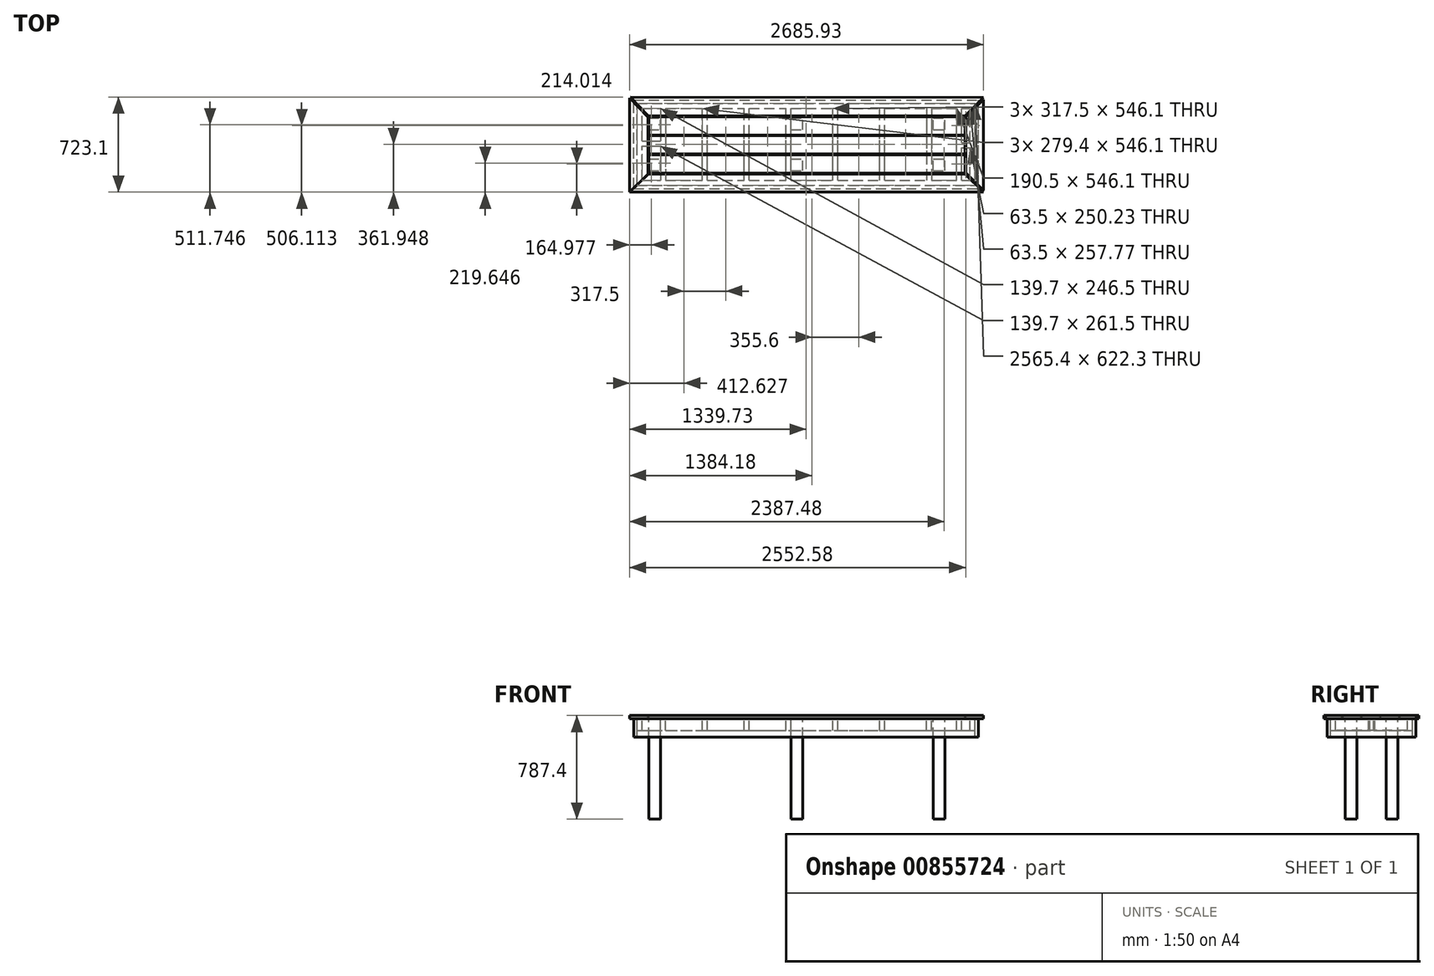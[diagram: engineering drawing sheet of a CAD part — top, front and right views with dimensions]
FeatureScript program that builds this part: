
annotation { "Feature Type Name" : "Feature", "Feature Type Description" : "" }
export const myFeature = defineFeature(function(context is Context, id is Id, definition is map)
    precondition{}
    {
        {
            var Q0;
            Q0=qCreatedBy(makeId("Top.planeOp"),FACE);
            var sketch = newSketch(context, id + "F0", { "sketchPlane" : qUnion([Q0])});
            skPoint(sketch, "E0.middle", {"position": v(0, 0) * mm});
            skLineSegment(sketch, "E1.bottom", {"start": v(-1467.07, -360.9) * mm, "end": v(1218.86, -360.9) * mm});
            skLineSegment(sketch, "E1.top", {"start": v(-1324.2, -222.85) * mm, "end": v(1080.8, -222.85) * mm});
            skLineSegment(sketch, "E2.0.1.0", {"start": v(-1321.05, -215.9) * mm, "end": v(1080.77, -215.9) * mm});
            skLineSegment(sketch, "E2.0.1.3", {"start": v(-1321.05, -76.2) * mm, "end": v(1080.04, -76.2) * mm});
            skLineSegment(sketch, "E2.0.2.0", {"start": v(-1321.05, -69.85) * mm, "end": v(1080, -69.85) * mm});
            skLineSegment(sketch, "E2.0.2.1", {"start": v(-1321.05, -69.85) * mm, "end": v(-1321.05, 69.85) * mm});
            skLineSegment(sketch, "E2.0.2.3", {"start": v(-1321.05, 69.85) * mm, "end": v(1079.27, 69.85) * mm});
            skLineSegment(sketch, "E2.0.3.0", {"start": v(-1321.05, 72.52) * mm, "end": v(1079.26, 72.52) * mm});
            skLineSegment(sketch, "E2.0.3.1", {"start": v(-1321.05, 72.52) * mm, "end": v(-1321.05, 210.28) * mm});
            skLineSegment(sketch, "E2.0.3.3", {"start": v(-1321.05, 210.28) * mm, "end": v(1078.53, 212.22) * mm});
            skLineSegment(sketch, "E2.0.4.0", {"start": v(-1322.9, 218.56) * mm, "end": v(1078.5, 218.56) * mm});
            skLineSegment(sketch, "E2.0.4.3", {"start": v(-1460.39, 362.2) * mm, "end": v(1218.86, 358.54) * mm});
            skLineSegment(sketch, "E3", {"start": v(-1321.05, -215.9) * mm, "end": v(-1321.05, -76.2) * mm});
            skLineSegment(sketch, "E4", {"start": v(-1467.07, -360.9) * mm, "end": v(-1324.2, -222.85) * mm});
            skLineSegment(sketch, "E5", {"start": v(-1326.9, -222.85) * mm, "end": v(-1467.07, -358.3) * mm});
            skLineSegment(sketch, "E6", {"start": v(-1467.07, 356.33) * mm, "end": v(-1467.07, -358.3) * mm});
            skLineSegment(sketch, "E7", {"start": v(-1327.27, 210.28) * mm, "end": v(-1467.07, 356.33) * mm});
            skLineSegment(sketch, "E8.trimOffspring", {"start": v(-1327.27, 210.28) * mm, "end": v(-1326.9, -222.85) * mm});
            skLineSegment(sketch, "E9", {"start": v(-1322.9, 218.56) * mm, "end": v(-1460.39, 362.2) * mm});
            skLineSegment(sketch, "E10", {"start": v(1218.86, -583.73) * mm, "end": v(1218.86, 490.14) * mm, "construction": true});
            skLineSegment(sketch, "E11", {"start": v(1218.86, -360.9) * mm, "end": v(1080.8, -222.85) * mm});
            skLineSegment(sketch, "E12", {"start": v(1218.86, 358.54) * mm, "end": v(1078.5, 218.56) * mm});
            skLineSegment(sketch, "E13", {"start": v(1080.77, -215.9) * mm, "end": v(1080.04, -76.2) * mm});
            skLineSegment(sketch, "E14.trimOffspring", {"start": v(1080, -69.85) * mm, "end": v(1079.27, 69.85) * mm});
            skLineSegment(sketch, "E15.trimOffspring", {"start": v(1079.26, 72.52) * mm, "end": v(1078.53, 212.22) * mm});
            skLineSegment(sketch, "E16", {"start": v(1086.83, -213.78) * mm, "end": v(1086.83, 211.28) * mm});
            skLineSegment(sketch, "E17", {"start": v(1086.83, 211.28) * mm, "end": v(1218.86, 342.95) * mm});
            skLineSegment(sketch, "E18", {"start": v(1086.83, -213.78) * mm, "end": v(1218.86, -345.8) * mm});
            skLineSegment(sketch, "E19", {"start": v(1218.86, -345.8) * mm, "end": v(1218.86, 342.95) * mm});
            skSolve(sketch);
        }
        {
            var Q0;
            Q0=makeQuery(id+"F0.imprint","IMPRINT",FACE,{"disambiguationData":[TD([[makeQuery(id+"F0.imprint","IMPRINT",EDGE,{"derivedFrom":sQuery(id+"F0.wireOp",EDGE,"HLl6yULO-rDhl-Czzw-94Pt-A62qj8Q72CLZ.bottom")}),-1.0]])]});
            var Q1;
            Q1=makeQuery(id+"F0.imprint","IMPRINT",FACE,{"disambiguationData":[TD([[makeQuery(id+"F0.imprint","IMPRINT",EDGE,{"derivedFrom":sQuery(id+"F0.wireOp",EDGE,"Z4ndjies-lr78-bC8g-xYQz-iFGjXOHwJ4Z8.bottom")}),1.0]])]});
            var Q2;
            Q2=makeQuery(id+"F0.imprint","IMPRINT",FACE,{"disambiguationData":[TD([[makeQuery(id+"F0.imprint","IMPRINT",EDGE,{"derivedFrom":sQuery(id+"F0.wireOp",EDGE,"E1.bottom")}),1.0]])]});
            var Q3;
            Q3=makeQuery(id+"F0.imprint","IMPRINT",FACE,{"disambiguationData":[TD([[makeQuery(id+"F0.imprint","IMPRINT",EDGE,{"derivedFrom":sQuery(id+"F0.wireOp",EDGE,"E2.0.1.0")}),1.0]])]});
            var Q4;
            Q4=makeQuery(id+"F0.imprint","IMPRINT",FACE,{"disambiguationData":[TD([[makeQuery(id+"F0.imprint","IMPRINT",EDGE,{"derivedFrom":sQuery(id+"F0.wireOp",EDGE,"E2.0.2.0")}),1.0]])]});
            var Q5;
            Q5=makeQuery(id+"F0.imprint","IMPRINT",FACE,{"disambiguationData":[TD([[makeQuery(id+"F0.imprint","IMPRINT",EDGE,{"derivedFrom":sQuery(id+"F0.wireOp",EDGE,"E2.0.3.0")}),1.0]])]});
            var Q6;
            Q6=makeQuery(id+"F0.imprint","IMPRINT",FACE,{"disambiguationData":[TD([[makeQuery(id+"F0.imprint","IMPRINT",EDGE,{"derivedFrom":sQuery(id+"F0.wireOp",EDGE,"E2.0.4.0")}),1.0]])]});
            var Q7;
            Q7=makeQuery(id+"F0.imprint","IMPRINT",FACE,{"disambiguationData":[TD([[makeQuery(id+"F0.imprint","IMPRINT",EDGE,{"derivedFrom":sQuery(id+"F0.wireOp",EDGE,"E5")}),-1.0]])]});
            var Q8;
            Q8=makeQuery(id+"F0.imprint","IMPRINT",FACE,{"disambiguationData":[TD([[makeQuery(id+"F0.imprint","IMPRINT",EDGE,{"derivedFrom":sQuery(id+"F0.wireOp",EDGE,"Z4ndjies-lr78-bC8g-xYQz-iFGjXOHwJ4Z8.left")}),-1.0]])]});
            var Q9;
            Q9=makeQuery(id+"F0.imprint","IMPRINT",FACE,{"disambiguationData":[TD([[makeQuery(id+"F0.imprint","IMPRINT",EDGE,{"derivedFrom":sQuery(id+"F0.wireOp",EDGE,"K0U2zqv0-DBfU-L3dn-5QTi-sevWSeDSVQ6E")}),1.0]])]});
            var Q10;
            Q10=makeQuery(id+"F0.imprint","IMPRINT",FACE,{"disambiguationData":[TD([[makeQuery(id+"F0.imprint","IMPRINT",EDGE,{"derivedFrom":sQuery(id+"F0.wireOp",EDGE,"E16")}),-1.0]])]});
            extrude(context, id + "F1", {"entities" : qUnion([Q0, Q1, Q2, Q3, Q4, Q5, Q6, Q7, Q8, Q9, Q10]), "oppositeDirection" : true, "depth" : 25.4 * mm, "offsetDistance" : 25.4 * mm});
        }
        {
            var Q0;
            Q0=makeQuery(id+"F1.opExtrude","CAP_FACE",FACE,{"disambiguationData":[OSD([sQuery(id+"F0.wireOp",EDGE,"E2.0.2.0"),sQuery(id+"F0.wireOp",EDGE,"E2.0.2.1"),sQuery(id+"F0.wireOp",EDGE,"E2.0.2.2"),sQuery(id+"F0.wireOp",EDGE,"E2.0.2.3")])],"isStart":false});
            var sketch = newSketch(context, id + "F2", { "sketchPlane" : qUnion([Q0])});
            skLineSegment(sketch, "E20.bottom", {"start": v(-1410.04, 310.1) * mm, "end": v(1155.36, 310.1) * mm});
            skLineSegment(sketch, "E20.top", {"start": v(-1410.04, -312.2) * mm, "end": v(1155.36, -312.2) * mm});
            skLineSegment(sketch, "E20.left", {"start": v(-1410.04, 310.1) * mm, "end": v(-1410.04, -312.2) * mm});
            skLineSegment(sketch, "E20.right", {"start": v(1155.36, 310.1) * mm, "end": v(1155.36, -312.2) * mm});
            skLineSegment(sketch, "E21.bottom", {"start": v(-1371.94, 272) * mm, "end": v(1117.26, 272) * mm});
            skLineSegment(sketch, "E21.top", {"start": v(-1371.94, -274.1) * mm, "end": v(1117.26, -274.1) * mm});
            skLineSegment(sketch, "E21.left", {"start": v(-1371.94, 272) * mm, "end": v(-1371.94, -274.1) * mm});
            skLineSegment(sketch, "E21.right", {"start": v(1117.26, 272) * mm, "end": v(1117.26, -274.1) * mm});
            skLineSegment(sketch, "E22.bottom", {"start": v(-1232.24, -274.1) * mm, "end": v(-1194.14, -274.1) * mm});
            skLineSegment(sketch, "E22.top", {"start": v(-1232.24, 272) * mm, "end": v(-1194.14, 272) * mm});
            skLineSegment(sketch, "E22.left", {"start": v(-1232.24, -274.1) * mm, "end": v(-1232.24, 272) * mm});
            skLineSegment(sketch, "E22.right", {"start": v(-1194.14, -274.1) * mm, "end": v(-1194.14, 272) * mm});
            skLineSegment(sketch, "E23.bottom", {"start": v(-88.93, -274.1) * mm, "end": v(-50.83, -274.1) * mm});
            skLineSegment(sketch, "E23.top", {"start": v(-88.93, 272) * mm, "end": v(-50.83, 272) * mm});
            skLineSegment(sketch, "E24.bottom", {"start": v(787.06, -274.1) * mm, "end": v(825.16, -274.1) * mm});
            skLineSegment(sketch, "E24.top", {"start": v(787.06, 272) * mm, "end": v(825.16, 272) * mm});
            skLineSegment(sketch, "E24.left", {"start": v(787.06, -274.1) * mm, "end": v(787.06, 272) * mm});
            skLineSegment(sketch, "E24.right", {"start": v(825.16, -274.1) * mm, "end": v(825.16, 272) * mm});
            skLineSegment(sketch, "E25.bottom", {"start": v(-914.74, 272) * mm, "end": v(-876.64, 272) * mm});
            skLineSegment(sketch, "E25.top", {"start": v(-914.74, -274.1) * mm, "end": v(-876.64, -274.1) * mm});
            skLineSegment(sketch, "E25.left", {"start": v(-914.74, 272) * mm, "end": v(-914.74, -274.1) * mm});
            skLineSegment(sketch, "E25.right", {"start": v(-876.64, 272) * mm, "end": v(-876.64, -274.1) * mm});
            skLineSegment(sketch, "E26.bottom", {"start": v(-279.74, 272) * mm, "end": v(-241.64, 272) * mm});
            skLineSegment(sketch, "E26.top", {"start": v(-279.74, -274.1) * mm, "end": v(-241.64, -274.1) * mm});
            skLineSegment(sketch, "E26.left", {"start": v(-279.74, 272) * mm, "end": v(-279.74, -274.1) * mm});
            skLineSegment(sketch, "E26.right", {"start": v(-241.64, 272) * mm, "end": v(-241.64, -274.1) * mm});
            skLineSegment(sketch, "E27.bottom", {"start": v(75.86, 272) * mm, "end": v(113.96, 272) * mm});
            skLineSegment(sketch, "E27.top", {"start": v(75.86, -274.1) * mm, "end": v(113.96, -274.1) * mm});
            skLineSegment(sketch, "E27.left", {"start": v(75.86, 272) * mm, "end": v(75.86, -274.1) * mm});
            skLineSegment(sketch, "E27.right", {"start": v(113.96, 272) * mm, "end": v(113.96, -274.1) * mm});
            skLineSegment(sketch, "E28.bottom", {"start": v(431.46, 272) * mm, "end": v(469.56, 272) * mm});
            skLineSegment(sketch, "E28.top", {"start": v(431.46, -274.1) * mm, "end": v(469.56, -274.1) * mm});
            skLineSegment(sketch, "E28.left", {"start": v(431.46, 272) * mm, "end": v(431.46, -274.1) * mm});
            skLineSegment(sketch, "E28.right", {"start": v(469.56, 272) * mm, "end": v(469.56, -274.1) * mm});
            skLineSegment(sketch, "E29.bottom", {"start": v(-1371.94, 272) * mm, "end": v(-1244.57, 272) * mm});
            skLineSegment(sketch, "E29.top", {"start": v(-1371.94, -274.1) * mm, "end": v(-1244.57, -274.1) * mm});
            skLineSegment(sketch, "E30.right", {"start": v(1117.26, 269.37) * mm, "end": v(1117.26, -274.1) * mm});
            skLineSegment(sketch, "E31.bottom", {"start": v(-597.24, 272) * mm, "end": v(-559.14, 272) * mm});
            skLineSegment(sketch, "E31.top", {"start": v(-597.24, -274.1) * mm, "end": v(-559.14, -274.1) * mm});
            skLineSegment(sketch, "E31.left", {"start": v(-597.24, 272) * mm, "end": v(-597.24, -274.1) * mm});
            skLineSegment(sketch, "E31.right", {"start": v(-559.14, 272) * mm, "end": v(-559.14, -274.1) * mm});
            skLineSegment(sketch, "E32.bottom", {"start": v(1015.66, 272) * mm, "end": v(1053.76, 272) * mm});
            skLineSegment(sketch, "E32.top", {"start": v(1015.66, -274.1) * mm, "end": v(1053.76, -274.1) * mm});
            skLineSegment(sketch, "E32.left", {"start": v(1015.66, 272) * mm, "end": v(1015.66, -274.1) * mm});
            skLineSegment(sketch, "E32.right", {"start": v(1053.76, 272) * mm, "end": v(1053.76, -274.1) * mm});
            skLineSegment(sketch, "E33.bottom", {"start": v(1053.76, 21.77) * mm, "end": v(1117.26, 21.77) * mm});
            skLineSegment(sketch, "E33.top", {"start": v(1053.76, -16.33) * mm, "end": v(1117.26, -16.33) * mm});
            skLineSegment(sketch, "E33.left", {"start": v(1053.76, 21.77) * mm, "end": v(1053.76, -16.33) * mm});
            skLineSegment(sketch, "E33.right", {"start": v(1117.26, 21.77) * mm, "end": v(1117.26, -16.33) * mm});
            skLineSegment(sketch, "E34.bottom", {"start": v(-1371.94, 10.5) * mm, "end": v(-1232.24, 10.5) * mm});
            skLineSegment(sketch, "E34.top", {"start": v(-1371.94, -27.6) * mm, "end": v(-1232.24, -27.6) * mm});
            skLineSegment(sketch, "E34.left", {"start": v(-1371.94, 10.5) * mm, "end": v(-1371.94, -27.6) * mm});
            skLineSegment(sketch, "E34.right", {"start": v(-1232.24, 10.5) * mm, "end": v(-1232.24, -27.6) * mm});
            skSolve(sketch);
        }
        {
            var Q0;
            Q0=makeQuery(id+"F2.imprint","IMPRINT",FACE,{"disambiguationData":[TD([[makeQuery(id+"F2.imprint","IMPRINT",EDGE,{"derivedFrom":sQuery(id+"F2.wireOp",EDGE,"E20.bottom")}),-1.0]])]});
            var Q1;
            {var subQ0=sQuery(id+"F2.wireOp",EDGE,"E22.left");var subQ1=sQuery(id+"F2.wireOp",EDGE,"E21.top");var subQ2=makeQuery(id+"F2.imprint","INTERSECT",VERTEX,{"derivedFrom":[subQ1,subQ0]});Q1=makeQuery(id+"F2.imprint","IMPRINT",FACE,{"disambiguationData":[TD([[makeQuery(id+"F2.imprint","IMPRINT",EDGE,{"disambiguationData":[TD([[subQ2,-1.0]])],"derivedFrom":subQ1}),1.0]])]});}
            var Q2;
            {var subQ5=sQuery(id+"F2.wireOp",EDGE,"E22.left");var subQ9=makeQuery(id+"F2.imprint","INTERSECT",VERTEX,{"derivedFrom":[subQ5,sQuery(id+"F2.wireOp",EDGE,"E34.bottom")]});Q2=makeQuery(id+"F2.imprint","IMPRINT",FACE,{"disambiguationData":[TD([[makeQuery(id+"F2.imprint","IMPRINT",EDGE,{"disambiguationData":[TD([[subQ9,-1.0]])],"derivedFrom":subQ5}),-1.0]])]});}
            var Q3;
            {var subQ0=sQuery(id+"F2.wireOp",EDGE,"E22.left");var subQ1=sQuery(id+"F2.wireOp",EDGE,"E21.bottom");var subQ2=makeQuery(id+"F2.imprint","INTERSECT",VERTEX,{"derivedFrom":[subQ1,subQ0]});Q3=makeQuery(id+"F2.imprint","IMPRINT",FACE,{"disambiguationData":[TD([[makeQuery(id+"F2.imprint","IMPRINT",EDGE,{"disambiguationData":[TD([[subQ2,-1.0]])],"derivedFrom":subQ1}),-1.0]])]});}
            var Q4;
            {var subQ0=sQuery(id+"F2.wireOp",EDGE,"E24.left");var subQ1=sQuery(id+"F2.wireOp",EDGE,"E21.top");var subQ2=makeQuery(id+"F2.imprint","INTERSECT",VERTEX,{"derivedFrom":[subQ1,subQ0]});Q4=makeQuery(id+"F2.imprint","IMPRINT",FACE,{"disambiguationData":[TD([[makeQuery(id+"F2.imprint","IMPRINT",EDGE,{"disambiguationData":[TD([[subQ2,-1.0]])],"derivedFrom":subQ1}),1.0]])]});}
            var Q5;
            {var subQ0=sQuery(id+"F2.wireOp",EDGE,"E24.left");var subQ1=makeQuery(id+"F1.opExtrude","CAP_EDGE",EDGE,{"disambiguationData":[OSD([sQuery(id+"F0.wireOp",EDGE,"E2.0.2.3")])],"isStart":false});var subQ2=makeQuery(id+"F2.imprint","INTERSECT",VERTEX,{"derivedFrom":[subQ1,subQ0]});Q5=makeQuery(id+"F2.imprint","IMPRINT",FACE,{"disambiguationData":[TD([[makeQuery(id+"F2.imprint","IMPRINT",EDGE,{"disambiguationData":[TD([[subQ2,-1.0]])],"derivedFrom":subQ0}),-1.0]])]});}
            var Q6;
            {var subQ0=sQuery(id+"F2.wireOp",EDGE,"E24.left");var subQ1=sQuery(id+"F2.wireOp",EDGE,"E21.bottom");var subQ2=makeQuery(id+"F2.imprint","INTERSECT",VERTEX,{"derivedFrom":[subQ1,subQ0]});Q6=makeQuery(id+"F2.imprint","IMPRINT",FACE,{"disambiguationData":[TD([[makeQuery(id+"F2.imprint","IMPRINT",EDGE,{"disambiguationData":[TD([[subQ2,-1.0]])],"derivedFrom":subQ1}),-1.0]])]});}
            var Q7;
            {var subQ0=sQuery(id+"F2.wireOp",EDGE,"E23.left");var subQ1=makeQuery(id+"F1.opExtrude","CAP_EDGE",EDGE,{"disambiguationData":[OSD([sQuery(id+"F0.wireOp",EDGE,"E2.0.2.3")])],"isStart":false});var subQ2=makeQuery(id+"F2.imprint","INTERSECT",VERTEX,{"derivedFrom":[subQ1,subQ0]});Q7=makeQuery(id+"F2.imprint","IMPRINT",FACE,{"disambiguationData":[TD([[makeQuery(id+"F2.imprint","IMPRINT",EDGE,{"disambiguationData":[TD([[subQ2,-1.0]])],"derivedFrom":subQ0}),-1.0]])]});}
            var Q8;
            {var subQ0=sQuery(id+"F2.wireOp",EDGE,"E25.left");var subQ1=sQuery(id+"F2.wireOp",EDGE,"E21.top");var subQ2=makeQuery(id+"F2.imprint","INTERSECT",VERTEX,{"derivedFrom":[subQ1,subQ0]});Q8=makeQuery(id+"F2.imprint","IMPRINT",FACE,{"disambiguationData":[TD([[makeQuery(id+"F2.imprint","IMPRINT",EDGE,{"disambiguationData":[TD([[subQ2,-1.0]])],"derivedFrom":subQ1}),1.0]])]});}
            var Q9;
            {var subQ0=sQuery(id+"F2.wireOp",EDGE,"E25.left");var subQ1=makeQuery(id+"F1.opExtrude","CAP_EDGE",EDGE,{"disambiguationData":[OSD([sQuery(id+"F0.wireOp",EDGE,"E2.0.2.0")])],"isStart":false});var subQ2=makeQuery(id+"F2.imprint","INTERSECT",VERTEX,{"derivedFrom":[subQ1,subQ0]});Q9=makeQuery(id+"F2.imprint","IMPRINT",FACE,{"disambiguationData":[TD([[makeQuery(id+"F2.imprint","IMPRINT",EDGE,{"disambiguationData":[TD([[subQ2,-1.0]])],"derivedFrom":subQ0}),1.0]])]});}
            var Q10;
            {var subQ0=sQuery(id+"F2.wireOp",EDGE,"E25.left");var subQ1=sQuery(id+"F2.wireOp",EDGE,"E21.bottom");var subQ2=makeQuery(id+"F2.imprint","INTERSECT",VERTEX,{"derivedFrom":[subQ1,subQ0]});Q10=makeQuery(id+"F2.imprint","IMPRINT",FACE,{"disambiguationData":[TD([[makeQuery(id+"F2.imprint","IMPRINT",EDGE,{"disambiguationData":[TD([[subQ2,-1.0]])],"derivedFrom":subQ1}),-1.0]])]});}
            var Q11;
            {var subQ0=sQuery(id+"F2.wireOp",EDGE,"E26.left");var subQ1=sQuery(id+"F2.wireOp",EDGE,"E21.top");var subQ2=makeQuery(id+"F2.imprint","INTERSECT",VERTEX,{"derivedFrom":[subQ1,subQ0]});Q11=makeQuery(id+"F2.imprint","IMPRINT",FACE,{"disambiguationData":[TD([[makeQuery(id+"F2.imprint","IMPRINT",EDGE,{"disambiguationData":[TD([[subQ2,-1.0]])],"derivedFrom":subQ1}),1.0]])]});}
            var Q12;
            {var subQ0=sQuery(id+"F2.wireOp",EDGE,"E26.left");var subQ1=makeQuery(id+"F1.opExtrude","CAP_EDGE",EDGE,{"disambiguationData":[OSD([sQuery(id+"F0.wireOp",EDGE,"E2.0.2.0")])],"isStart":false});var subQ2=makeQuery(id+"F2.imprint","INTERSECT",VERTEX,{"derivedFrom":[subQ1,subQ0]});Q12=makeQuery(id+"F2.imprint","IMPRINT",FACE,{"disambiguationData":[TD([[makeQuery(id+"F2.imprint","IMPRINT",EDGE,{"disambiguationData":[TD([[subQ2,-1.0]])],"derivedFrom":subQ0}),1.0]])]});}
            var Q13;
            {var subQ0=sQuery(id+"F2.wireOp",EDGE,"E26.left");var subQ1=sQuery(id+"F2.wireOp",EDGE,"E21.bottom");var subQ2=makeQuery(id+"F2.imprint","INTERSECT",VERTEX,{"derivedFrom":[subQ1,subQ0]});Q13=makeQuery(id+"F2.imprint","IMPRINT",FACE,{"disambiguationData":[TD([[makeQuery(id+"F2.imprint","IMPRINT",EDGE,{"disambiguationData":[TD([[subQ2,-1.0]])],"derivedFrom":subQ1}),-1.0]])]});}
            var Q14;
            {var subQ0=sQuery(id+"F2.wireOp",EDGE,"E27.left");var subQ1=sQuery(id+"F2.wireOp",EDGE,"E21.top");var subQ2=makeQuery(id+"F2.imprint","INTERSECT",VERTEX,{"derivedFrom":[subQ1,subQ0]});Q14=makeQuery(id+"F2.imprint","IMPRINT",FACE,{"disambiguationData":[TD([[makeQuery(id+"F2.imprint","IMPRINT",EDGE,{"disambiguationData":[TD([[subQ2,-1.0]])],"derivedFrom":subQ1}),1.0]])]});}
            var Q15;
            {var subQ0=sQuery(id+"F2.wireOp",EDGE,"E27.left");var subQ1=makeQuery(id+"F1.opExtrude","CAP_EDGE",EDGE,{"disambiguationData":[OSD([sQuery(id+"F0.wireOp",EDGE,"E2.0.2.0")])],"isStart":false});var subQ2=makeQuery(id+"F2.imprint","INTERSECT",VERTEX,{"derivedFrom":[subQ1,subQ0]});Q15=makeQuery(id+"F2.imprint","IMPRINT",FACE,{"disambiguationData":[TD([[makeQuery(id+"F2.imprint","IMPRINT",EDGE,{"disambiguationData":[TD([[subQ2,-1.0]])],"derivedFrom":subQ0}),1.0]])]});}
            var Q16;
            {var subQ0=sQuery(id+"F2.wireOp",EDGE,"E27.right");var subQ1=sQuery(id+"F2.wireOp",EDGE,"E21.bottom");var subQ2=makeQuery(id+"F2.imprint","INTERSECT",VERTEX,{"derivedFrom":[subQ1,subQ0]});Q16=makeQuery(id+"F2.imprint","IMPRINT",FACE,{"disambiguationData":[TD([[makeQuery(id+"F2.imprint","IMPRINT",EDGE,{"disambiguationData":[TD([[subQ2,1.0]])],"derivedFrom":subQ1}),-1.0]])]});}
            var Q17;
            {var subQ0=sQuery(id+"F2.wireOp",EDGE,"E28.right");var subQ1=sQuery(id+"F2.wireOp",EDGE,"E21.top");var subQ2=makeQuery(id+"F2.imprint","INTERSECT",VERTEX,{"derivedFrom":[subQ1,subQ0]});Q17=makeQuery(id+"F2.imprint","IMPRINT",FACE,{"disambiguationData":[TD([[makeQuery(id+"F2.imprint","IMPRINT",EDGE,{"disambiguationData":[TD([[subQ2,1.0]])],"derivedFrom":subQ1}),1.0]])]});}
            var Q18;
            {var subQ0=sQuery(id+"F2.wireOp",EDGE,"E28.left");var subQ1=makeQuery(id+"F1.opExtrude","CAP_EDGE",EDGE,{"disambiguationData":[OSD([sQuery(id+"F0.wireOp",EDGE,"E2.0.2.0")])],"isStart":false});var subQ2=makeQuery(id+"F2.imprint","INTERSECT",VERTEX,{"derivedFrom":[subQ1,subQ0]});Q18=makeQuery(id+"F2.imprint","IMPRINT",FACE,{"disambiguationData":[TD([[makeQuery(id+"F2.imprint","IMPRINT",EDGE,{"disambiguationData":[TD([[subQ2,-1.0]])],"derivedFrom":subQ0}),1.0]])]});}
            var Q19;
            {var subQ0=sQuery(id+"F2.wireOp",EDGE,"E28.left");var subQ1=sQuery(id+"F2.wireOp",EDGE,"E21.bottom");var subQ2=makeQuery(id+"F2.imprint","INTERSECT",VERTEX,{"derivedFrom":[subQ1,subQ0]});Q19=makeQuery(id+"F2.imprint","IMPRINT",FACE,{"disambiguationData":[TD([[makeQuery(id+"F2.imprint","IMPRINT",EDGE,{"disambiguationData":[TD([[subQ2,-1.0]])],"derivedFrom":subQ1}),-1.0]])]});}
            var Q20;
            {var subQ0=sQuery(id+"F2.wireOp",EDGE,"E31.left");var subQ1=sQuery(id+"F2.wireOp",EDGE,"E21.top");var subQ2=makeQuery(id+"F2.imprint","INTERSECT",VERTEX,{"derivedFrom":[subQ1,subQ0]});Q20=makeQuery(id+"F2.imprint","IMPRINT",FACE,{"disambiguationData":[TD([[makeQuery(id+"F2.imprint","IMPRINT",EDGE,{"disambiguationData":[TD([[subQ2,-1.0]])],"derivedFrom":subQ1}),1.0]])]});}
            var Q21;
            {var subQ0=sQuery(id+"F2.wireOp",EDGE,"E31.left");var subQ1=makeQuery(id+"F1.opExtrude","CAP_EDGE",EDGE,{"disambiguationData":[OSD([sQuery(id+"F0.wireOp",EDGE,"E2.0.2.0")])],"isStart":false});var subQ2=makeQuery(id+"F2.imprint","INTERSECT",VERTEX,{"derivedFrom":[subQ1,subQ0]});Q21=makeQuery(id+"F2.imprint","IMPRINT",FACE,{"disambiguationData":[TD([[makeQuery(id+"F2.imprint","IMPRINT",EDGE,{"disambiguationData":[TD([[subQ2,-1.0]])],"derivedFrom":subQ0}),1.0]])]});}
            var Q22;
            {var subQ0=sQuery(id+"F2.wireOp",EDGE,"E31.left");var subQ1=sQuery(id+"F2.wireOp",EDGE,"E21.bottom");var subQ2=makeQuery(id+"F2.imprint","INTERSECT",VERTEX,{"derivedFrom":[subQ1,subQ0]});Q22=makeQuery(id+"F2.imprint","IMPRINT",FACE,{"disambiguationData":[TD([[makeQuery(id+"F2.imprint","IMPRINT",EDGE,{"disambiguationData":[TD([[subQ2,-1.0]])],"derivedFrom":subQ1}),-1.0]])]});}
            var Q23;
            {var subQ0=sQuery(id+"F2.wireOp",EDGE,"E32.left");var subQ1=sQuery(id+"F2.wireOp",EDGE,"E21.top");var subQ2=makeQuery(id+"F2.imprint","INTERSECT",VERTEX,{"derivedFrom":[subQ1,subQ0]});Q23=makeQuery(id+"F2.imprint","IMPRINT",FACE,{"disambiguationData":[TD([[makeQuery(id+"F2.imprint","IMPRINT",EDGE,{"disambiguationData":[TD([[subQ2,-1.0]])],"derivedFrom":subQ1}),1.0]])]});}
            var Q24;
            {var subQ2=makeQuery(id+"F1.opExtrude","CAP_EDGE",EDGE,{"disambiguationData":[OSD([sQuery(id+"F0.wireOp",EDGE,"E2.0.2.0")])],"isStart":false});var subQ4=sQuery(id+"F2.wireOp",EDGE,"E32.left");var subQ5=makeQuery(id+"F2.imprint","INTERSECT",VERTEX,{"derivedFrom":[subQ2,subQ4]});Q24=makeQuery(id+"F2.imprint","IMPRINT",FACE,{"disambiguationData":[TD([[makeQuery(id+"F2.imprint","IMPRINT",EDGE,{"disambiguationData":[TD([[subQ5,-1.0]])],"derivedFrom":subQ4}),1.0]])]});}
            var Q25;
            {var subQ0=sQuery(id+"F2.wireOp",EDGE,"E32.left");var subQ1=sQuery(id+"F2.wireOp",EDGE,"E21.bottom");var subQ2=makeQuery(id+"F2.imprint","INTERSECT",VERTEX,{"derivedFrom":[subQ1,subQ0]});Q25=makeQuery(id+"F2.imprint","IMPRINT",FACE,{"disambiguationData":[TD([[makeQuery(id+"F2.imprint","IMPRINT",EDGE,{"disambiguationData":[TD([[subQ2,-1.0]])],"derivedFrom":subQ1}),-1.0]])]});}
            var Q26;
            {var subQ0=sQuery(id+"F2.wireOp",EDGE,"E34.bottom");var subQ1=sQuery(id+"F2.wireOp",EDGE,"E22.left");var subQ2=makeQuery(id+"F2.imprint","INTERSECT",VERTEX,{"derivedFrom":[subQ1,subQ0]});Q26=makeQuery(id+"F2.imprint","IMPRINT",FACE,{"disambiguationData":[TD([[makeQuery(id+"F2.imprint","IMPRINT",EDGE,{"disambiguationData":[TD([[subQ2,1.0]])],"derivedFrom":subQ1}),1.0]])]});}
            var Q27;
            {var subQ0=sQuery(id+"F2.wireOp",EDGE,"E34.top");var subQ1=sQuery(id+"F2.wireOp",EDGE,"E21.left");var subQ2=makeQuery(id+"F2.imprint","INTERSECT",VERTEX,{"derivedFrom":[subQ1,subQ0]});Q27=makeQuery(id+"F2.imprint","IMPRINT",FACE,{"disambiguationData":[TD([[makeQuery(id+"F2.imprint","IMPRINT",EDGE,{"disambiguationData":[TD([[subQ2,1.0]])],"derivedFrom":subQ1}),1.0]])]});}
            var Q28;
            {var subQ0=sQuery(id+"F2.wireOp",EDGE,"E33.top");var subQ1=sQuery(id+"F2.wireOp",EDGE,"E32.right");var subQ2=makeQuery(id+"F2.imprint","INTERSECT",VERTEX,{"derivedFrom":[subQ1,subQ0]});Q28=makeQuery(id+"F2.imprint","IMPRINT",FACE,{"disambiguationData":[TD([[makeQuery(id+"F2.imprint","IMPRINT",EDGE,{"disambiguationData":[TD([[subQ2,1.0]])],"derivedFrom":subQ1}),1.0]])]});}
            var Q29;
            {var subQ0=sQuery(id+"F2.wireOp",EDGE,"E33.top");var subQ1=sQuery(id+"F2.wireOp",EDGE,"E21.right");var subQ2=makeQuery(id+"F2.imprint","INTERSECT",VERTEX,{"derivedFrom":[subQ1,subQ0]});Q29=makeQuery(id+"F2.imprint","IMPRINT",FACE,{"disambiguationData":[TD([[makeQuery(id+"F2.imprint","IMPRINT",EDGE,{"disambiguationData":[TD([[subQ2,1.0]])],"derivedFrom":subQ1}),-1.0]])]});}
            extrude(context, id + "F3", {"entities" : qUnion([Q0, Q1, Q2, Q3, Q4, Q5, Q6, Q7, Q8, Q9, Q10, Q11, Q12, Q13, Q14, Q15, Q16, Q17, Q18, Q19, Q20, Q21, Q22, Q23, Q24, Q25, Q26, Q27, Q28, Q29]), "depth" : 88.9 * mm, "offsetDistance" : 25.4 * mm});
        }
        {
            var Q0;
            {var subQ0=sQuery(id+"F2.wireOp",EDGE,"E28.left");var subQ1=sQuery(id+"F2.wireOp",EDGE,"E21.bottom");var subQ2=makeQuery(id+"F2.imprint","INTERSECT",VERTEX,{"derivedFrom":[subQ1,subQ0]});var subQ10=sQuery(id+"F2.wireOp",EDGE,"E32.left");var subQ11=makeQuery(id+"F2.imprint","INTERSECT",VERTEX,{"derivedFrom":[subQ1,subQ10]});var subQ17=sQuery(id+"F2.wireOp",EDGE,"E26.left");var subQ18=makeQuery(id+"F2.imprint","INTERSECT",VERTEX,{"derivedFrom":[subQ1,subQ17]});var subQ25=sQuery(id+"F2.wireOp",EDGE,"E24.left");var subQ26=makeQuery(id+"F2.imprint","INTERSECT",VERTEX,{"derivedFrom":[subQ1,subQ25]});var subQ27=sQuery(id+"F2.wireOp",EDGE,"E24.right");var subQ28=makeQuery(id+"F2.imprint","INTERSECT",VERTEX,{"derivedFrom":[subQ1,subQ27]});var subQ33=sQuery(id+"F2.wireOp",EDGE,"E31.left");var subQ34=makeQuery(id+"F2.imprint","INTERSECT",VERTEX,{"derivedFrom":[subQ1,subQ33]});var subQ37=sQuery(id+"F2.wireOp",EDGE,"E25.right");var subQ38=makeQuery(id+"F2.imprint","INTERSECT",VERTEX,{"derivedFrom":[subQ1,subQ37]});var subQ41=sQuery(id+"F2.wireOp",EDGE,"E25.left");var subQ42=makeQuery(id+"F2.imprint","INTERSECT",VERTEX,{"derivedFrom":[subQ1,subQ41]});var subQ45=sQuery(id+"F2.wireOp",EDGE,"E22.right");var subQ46=makeQuery(id+"F2.imprint","INTERSECT",VERTEX,{"derivedFrom":[subQ1,subQ45]});var subQ52=sQuery(id+"F2.wireOp",EDGE,"E22.left");var subQ53=makeQuery(id+"F2.imprint","INTERSECT",VERTEX,{"derivedFrom":[subQ1,subQ52]});var subQ55=sQuery(id+"F2.wireOp",EDGE,"E27.right");var subQ56=makeQuery(id+"F2.imprint","INTERSECT",VERTEX,{"derivedFrom":[subQ1,subQ55]});Q0=qUnion([makeQuery(id+"F2.imprint","IMPRINT",FACE,{"disambiguationData":[TD([[makeQuery(id+"F2.imprint","IMPRINT",EDGE,{"disambiguationData":[TD([[subQ28,-1.0]])],"derivedFrom":subQ1}),-1.0]])]}),makeQuery(id+"F2.imprint","IMPRINT",FACE,{"disambiguationData":[TD([[makeQuery(id+"F2.imprint","IMPRINT",EDGE,{"disambiguationData":[TD([[subQ56,-1.0]])],"derivedFrom":subQ1}),-1.0]])]}),makeQuery(id+"F2.imprint","IMPRINT",FACE,{"disambiguationData":[TD([[makeQuery(id+"F2.imprint","IMPRINT",EDGE,{"disambiguationData":[TD([[subQ56,1.0]])],"derivedFrom":subQ1}),-1.0]])]}),makeQuery(id+"F2.imprint","IMPRINT",FACE,{"disambiguationData":[TD([[makeQuery(id+"F2.imprint","IMPRINT",EDGE,{"disambiguationData":[TD([[subQ26,1.0]])],"derivedFrom":subQ1}),-1.0]])]}),makeQuery(id+"F2.imprint","IMPRINT",FACE,{"disambiguationData":[TD([[makeQuery(id+"F2.imprint","IMPRINT",EDGE,{"disambiguationData":[TD([[subQ53,-1.0]])],"derivedFrom":subQ1}),-1.0]])]}),makeQuery(id+"F2.imprint","IMPRINT",FACE,{"disambiguationData":[TD([[makeQuery(id+"F2.imprint","IMPRINT",EDGE,{"disambiguationData":[TD([[subQ18,-1.0]])],"derivedFrom":subQ1}),-1.0]])]}),makeQuery(id+"F2.imprint","IMPRINT",FACE,{"disambiguationData":[TD([[makeQuery(id+"F2.imprint","IMPRINT",EDGE,{"disambiguationData":[TD([[subQ46,-1.0]])],"derivedFrom":subQ1}),-1.0]])]}),makeQuery(id+"F2.imprint","IMPRINT",FACE,{"disambiguationData":[TD([[makeQuery(id+"F2.imprint","IMPRINT",EDGE,{"disambiguationData":[TD([[subQ42,-1.0]])],"derivedFrom":subQ1}),-1.0]])]}),makeQuery(id+"F2.imprint","IMPRINT",FACE,{"disambiguationData":[TD([[makeQuery(id+"F2.imprint","IMPRINT",EDGE,{"disambiguationData":[TD([[subQ38,-1.0]])],"derivedFrom":subQ1}),-1.0]])]}),makeQuery(id+"F2.imprint","IMPRINT",FACE,{"disambiguationData":[TD([[makeQuery(id+"F2.imprint","IMPRINT",EDGE,{"disambiguationData":[TD([[subQ34,-1.0]])],"derivedFrom":subQ1}),-1.0]])]}),makeQuery(id+"F2.imprint","IMPRINT",FACE,{"disambiguationData":[TD([[makeQuery(id+"F2.imprint","IMPRINT",EDGE,{"disambiguationData":[TD([[subQ26,-1.0]])],"derivedFrom":subQ1}),-1.0]])]}),makeQuery(id+"F2.imprint","IMPRINT",FACE,{"disambiguationData":[TD([[makeQuery(id+"F2.imprint","IMPRINT",EDGE,{"disambiguationData":[TD([[subQ18,1.0]])],"derivedFrom":subQ1}),-1.0]])]}),makeQuery(id+"F2.imprint","IMPRINT",FACE,{"disambiguationData":[TD([[makeQuery(id+"F2.imprint","IMPRINT",EDGE,{"disambiguationData":[TD([[subQ11,-1.0]])],"derivedFrom":subQ1}),-1.0]])]}),makeQuery(id+"F2.imprint","IMPRINT",FACE,{"disambiguationData":[TD([[makeQuery(id+"F2.imprint","IMPRINT",EDGE,{"disambiguationData":[TD([[subQ2,-1.0]])],"derivedFrom":subQ1}),-1.0]])]})]);}
            var sketch = newSketch(context, id + "F4", { "sketchPlane" : qUnion([Q0])});
            skLineSegment(sketch, "E35.bottom", {"start": v(-1321.14, 197.58) * mm, "end": v(-1232.24, 197.58) * mm});
            skLineSegment(sketch, "E35.top", {"start": v(-1321.14, 108.68) * mm, "end": v(-1232.24, 108.68) * mm});
            skLineSegment(sketch, "E35.left", {"start": v(-1321.14, 197.58) * mm, "end": v(-1321.14, 108.68) * mm});
            skLineSegment(sketch, "E35.right", {"start": v(-1232.24, 197.58) * mm, "end": v(-1232.24, 108.68) * mm});
            skLineSegment(sketch, "E36.0.1.0", {"start": v(-1321.14, -112.3) * mm, "end": v(-1321.14, -201.2) * mm});
            skLineSegment(sketch, "E36.0.1.1", {"start": v(-1321.14, -112.3) * mm, "end": v(-1232.24, -112.3) * mm});
            skLineSegment(sketch, "E36.0.1.2", {"start": v(-1232.24, -112.3) * mm, "end": v(-1232.24, -201.2) * mm});
            skLineSegment(sketch, "E36.0.1.3", {"start": v(-1321.14, -201.2) * mm, "end": v(-1232.24, -201.2) * mm});
            skLineSegment(sketch, "E36.1.0.0", {"start": v(-241.64, 197.58) * mm, "end": v(-241.64, 108.68) * mm});
            skLineSegment(sketch, "E36.1.0.1", {"start": v(-241.64, 197.58) * mm, "end": v(-152.74, 197.58) * mm});
            skLineSegment(sketch, "E36.1.0.2", {"start": v(-152.74, 197.58) * mm, "end": v(-152.74, 108.68) * mm});
            skLineSegment(sketch, "E36.1.0.3", {"start": v(-241.64, 108.68) * mm, "end": v(-152.74, 108.68) * mm});
            skLineSegment(sketch, "E36.1.1.0", {"start": v(-241.64, -112.3) * mm, "end": v(-241.64, -201.2) * mm});
            skLineSegment(sketch, "E36.1.1.1", {"start": v(-241.64, -112.3) * mm, "end": v(-152.74, -112.3) * mm});
            skLineSegment(sketch, "E36.1.1.2", {"start": v(-152.74, -112.3) * mm, "end": v(-152.74, -201.2) * mm});
            skLineSegment(sketch, "E36.1.1.3", {"start": v(-241.64, -201.2) * mm, "end": v(-152.74, -201.2) * mm});
            skLineSegment(sketch, "E36.2.0.0", {"start": v(837.86, 197.58) * mm, "end": v(837.86, 108.68) * mm});
            skLineSegment(sketch, "E36.2.0.1", {"start": v(837.86, 197.58) * mm, "end": v(926.76, 197.58) * mm});
            skLineSegment(sketch, "E36.2.0.2", {"start": v(926.76, 197.58) * mm, "end": v(926.76, 108.68) * mm});
            skLineSegment(sketch, "E36.2.0.3", {"start": v(837.86, 108.68) * mm, "end": v(926.76, 108.68) * mm});
            skLineSegment(sketch, "E36.2.1.0", {"start": v(837.86, -112.3) * mm, "end": v(837.86, -201.2) * mm});
            skLineSegment(sketch, "E36.2.1.1", {"start": v(837.86, -112.3) * mm, "end": v(926.76, -112.3) * mm});
            skLineSegment(sketch, "E36.2.1.2", {"start": v(926.76, -112.3) * mm, "end": v(926.76, -201.2) * mm});
            skLineSegment(sketch, "E36.2.1.3", {"start": v(837.86, -201.2) * mm, "end": v(926.76, -201.2) * mm});
            skLineSegment(sketch, "E36.direction1", {"start": v(-1321.14, 108.68) * mm, "end": v(-241.64, 108.68) * mm, "construction": true});
            skLineSegment(sketch, "E36.direction2", {"start": v(-1321.14, 108.68) * mm, "end": v(-1321.14, -201.2) * mm, "construction": true});
            skSolve(sketch);
        }
        {
            var Q0;
            Q0 = qSketchRegion(id + "F4", true);
            extrude(context, id + "F5", {"entities" : qUnion([Q0]), "depth" : 762 * mm, "offsetDistance" : 25.4 * mm});
        }
        {
            var Q0;
            Q0=makeQuery(id+"F1.opExtrude","CAP_FACE",FACE,{"disambiguationData":[OSD([sQuery(id+"F0.wireOp",EDGE,"E1.bottom"),sQuery(id+"F0.wireOp",EDGE,"E1.top"),sQuery(id+"F0.wireOp",EDGE,"E4"),sQuery(id+"F0.wireOp",EDGE,"E11")])],"isStart":false});
            var sketch = newSketch(context, id + "F6", { "sketchPlane" : qUnion([Q0])});
            skLineSegment(sketch, "E37.0", {"start": v(-1410.04, 310.1) * mm, "end": v(1155.36, 310.1) * mm});
            skLineSegment(sketch, "E38.0", {"start": v(-1410.04, 310.1) * mm, "end": v(-1410.04, -312.2) * mm});
            skLineSegment(sketch, "E39.0", {"start": v(-1410.04, -312.2) * mm, "end": v(1155.36, -312.2) * mm});
            skLineSegment(sketch, "E40.0", {"start": v(1155.36, 310.1) * mm, "end": v(1155.36, -312.2) * mm});
            skLineSegment(sketch, "E41.0", {"start": v(-1435.44, 335.5) * mm, "end": v(1180.76, 335.5) * mm});
            skLineSegment(sketch, "E41.1", {"start": v(-1435.44, 335.5) * mm, "end": v(-1435.44, -337.6) * mm});
            skLineSegment(sketch, "E41.2", {"start": v(-1435.44, -337.6) * mm, "end": v(1180.76, -337.6) * mm});
            skLineSegment(sketch, "E41.3", {"start": v(1180.76, 335.5) * mm, "end": v(1180.76, -337.6) * mm});
            skSolve(sketch);
        }
        {
            var Q0;
            {var subQ1=sQuery(id+"F6.wireOp",EDGE,"E37.0");Q0=makeQuery(id+"F6.imprint","IMPRINT",FACE,{"disambiguationData":[TD([[makeQuery(id+"F6.imprint","IMPRINT",EDGE,{"derivedFrom":subQ1}),1.0]])]});}
            var Q1;
            {var subQ1=sQuery(id+"F6.wireOp",EDGE,"E39.0");Q1=makeQuery(id+"F6.imprint","IMPRINT",FACE,{"disambiguationData":[TD([[makeQuery(id+"F6.imprint","IMPRINT",EDGE,{"derivedFrom":subQ1}),-1.0]])]});}
            extrude(context, id + "F7", {"entities" : qUnion([Q0, Q1]), "depth" : 139.7 * mm, "offsetDistance" : 25.4 * mm});
        }
    });
